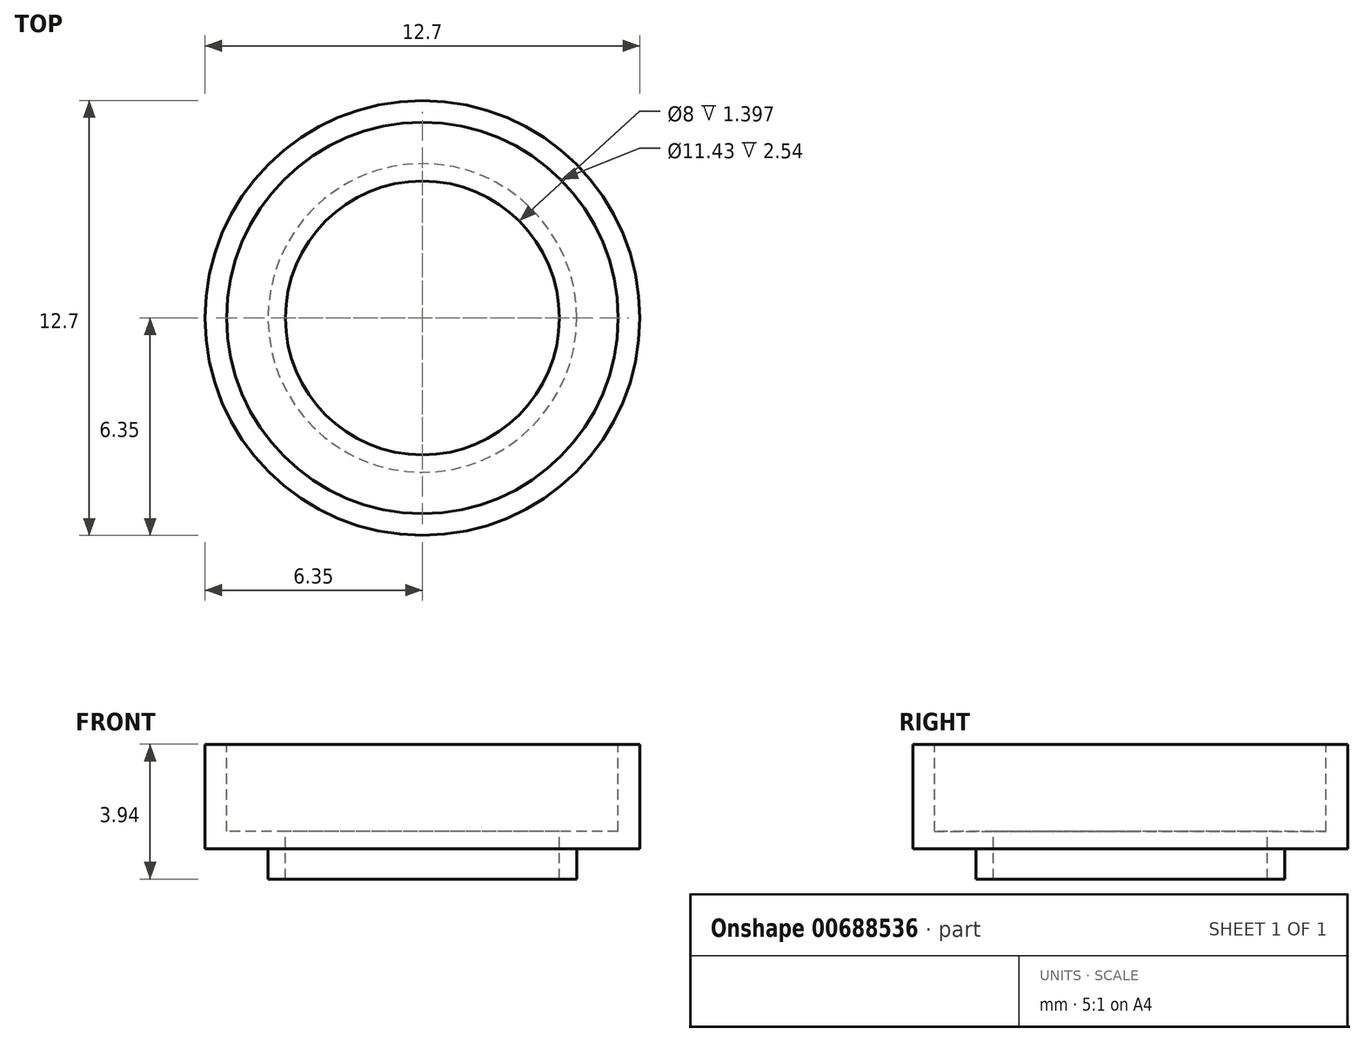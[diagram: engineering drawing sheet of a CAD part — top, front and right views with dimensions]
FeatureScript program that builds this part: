
annotation { "Feature Type Name" : "Feature", "Feature Type Description" : "" }
export const myFeature = defineFeature(function(context is Context, id is Id, definition is map)
    precondition{}
    {
        {
            var Q0;
            Q0=qCreatedBy(makeId("Top.planeOp"),FACE);
            var sketch = newSketch(context, id + "F0", { "sketchPlane" : qUnion([Q0])});
            skCircle(sketch, "E0", {"center": v(0, 0) * mm, "radius": 4.5 * mm});
            skSolve(sketch);
        }
        {
            var Q0;
            Q0 = qSketchRegion(id + "F0", true);
            extrude(context, id + "F1", {"entities" : qUnion([Q0]), "oppositeDirection" : true, "depth" : 0.89 * mm, "offsetDistance" : 25.4 * mm});
        }
        {
            var Q0;
            Q0=makeQuery(id+"F1.opExtrude","CAP_FACE",FACE,{"disambiguationData":[OSD([sQuery(id+"F0.wireOp",EDGE,"E0")])],"isStart":true});
            var sketch = newSketch(context, id + "F2", { "sketchPlane" : qUnion([Q0])});
            skCircle(sketch, "E1", {"center": v(0, 0) * mm, "radius": 6.35 * mm});
            skSolve(sketch);
        }
        {
            var Q0;
            Q0=makeQuery(id+"F2.imprint","IMPRINT",FACE,{"disambiguationData":[TD([[makeQuery(id+"F2.imprint","IMPRINT",EDGE,{"derivedFrom":makeQuery(id+"F1.opExtrude","CAP_EDGE",EDGE,{"disambiguationData":[OSD([sQuery(id+"F0.wireOp",EDGE,"E0")])],"isStart":true})}),1.0]])]});
            var sketch = newSketch(context, id + "F3", { "sketchPlane" : qUnion([Q0])});
            skCircle(sketch, "E2", {"center": v(0, 0) * mm, "radius": 4 * mm});
            skSolve(sketch);
        }
        {
            var Q0;
            Q0 = qSketchRegion(id + "F2", true);
            extrude(context, id + "F4", {"entities" : qUnion([Q0]), "operationType" : NewBodyOperationType.ADD, "depth" : 3.05 * mm, "offsetDistance" : 25.4 * mm});
        }
        {
            var Q0;
            Q0=makeQuery(id+"F4.opExtrude","CAP_FACE",FACE,{"disambiguationData":[OSD([sQuery(id+"F2.wireOp",EDGE,"E1")])],"isStart":false});
            var sketch = newSketch(context, id + "F5", { "sketchPlane" : qUnion([Q0])});
            skCircle(sketch, "E3", {"center": v(0, 0) * mm, "radius": 5.72 * mm});
            skSolve(sketch);
        }
        {
            var Q0;
            Q0 = qSketchRegion(id + "F3", true);
            extrude(context, id + "F6", {"entities" : qUnion([Q0]), "operationType" : NewBodyOperationType.REMOVE, "endBound" : BoundingType.SYMMETRIC, "oppositeDirection" : true, "depth" : 21.34 * mm, "offsetDistance" : 25.4 * mm});
        }
        {
            var Q0;
            Q0 = qSketchRegion(id + "F5", true);
            extrude(context, id + "F7", {"entities" : qUnion([Q0]), "operationType" : NewBodyOperationType.REMOVE, "oppositeDirection" : true, "depth" : 2.54 * mm, "offsetDistance" : 25.4 * mm});
        }
    });
